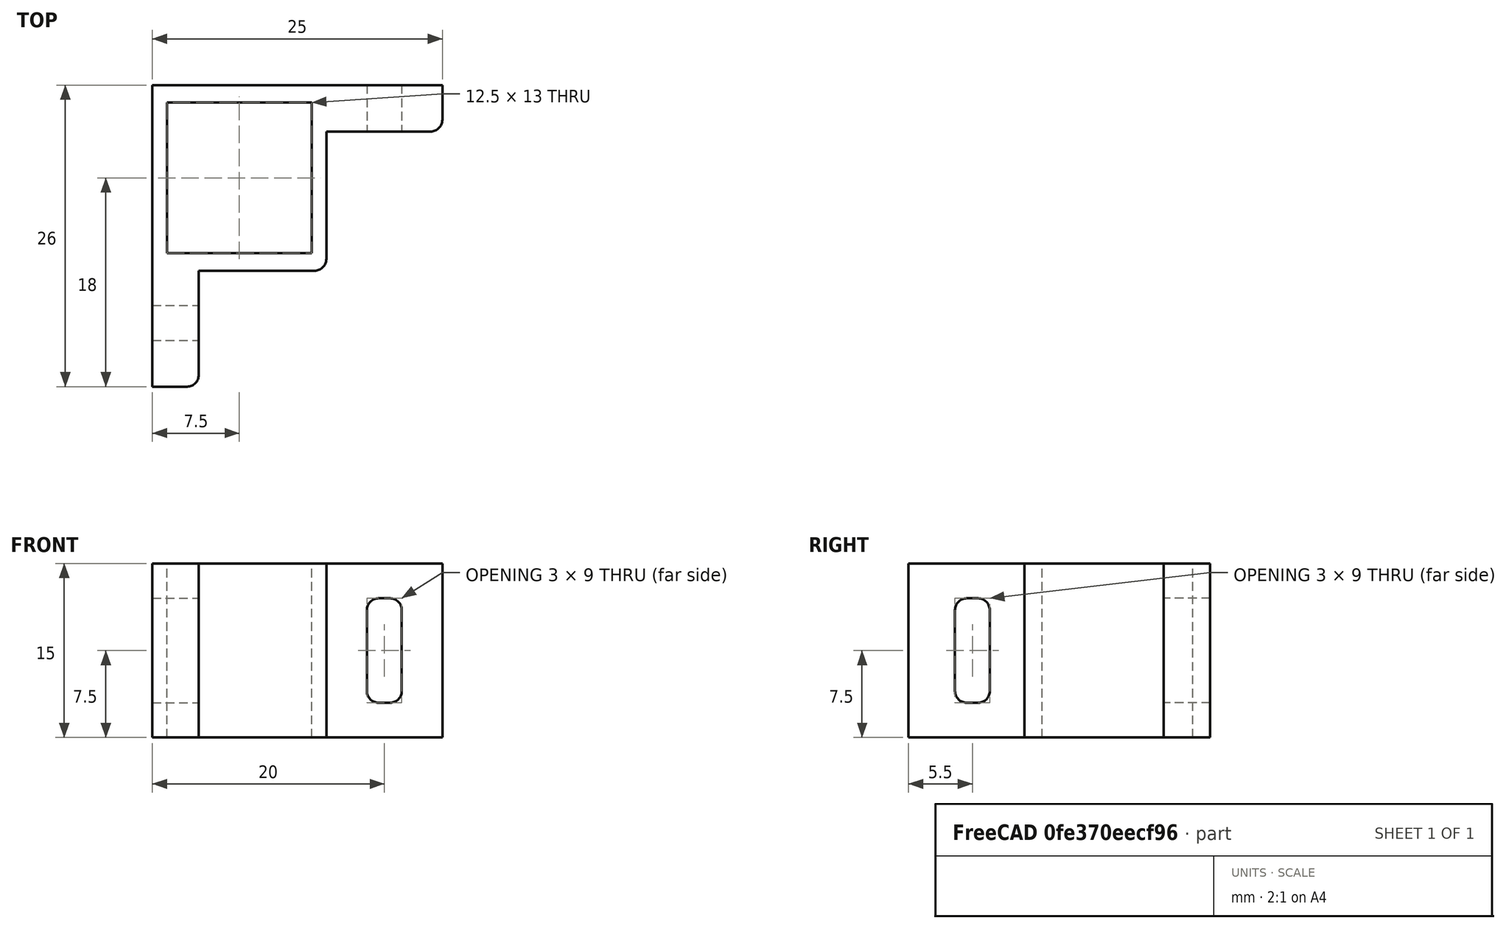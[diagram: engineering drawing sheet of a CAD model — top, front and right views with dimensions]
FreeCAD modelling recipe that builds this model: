
FCSTD DOCUMENT  (FreeCAD 0.14R3402 (Git))
Label: DoorSwitchClamp
License: CC-BY 3.0
LicenseURL: http://creativecommons.org/licenses/by/3.0/
objects: Part::Box×6, Part::Fillet×5, Part::Cut×3, Part::MultiFuse×1
note: 15 computed .brp shape members not serialized (recipe doc carries the construction recipe); baked Part::Feature solids carry a one-line shape summary decoded from their .brp

FEATURE [Part::Box] Box  label="Cube"
  Height = 16
  Length = 15
  Width = 15
FEATURE [Part::Box] Box001  label="Cube001"
  Height = 13
  Length = 12.5
  Placement = pos=(1.25,0,1.5) rot=(0,0,1;0rad)
  Width = 15
FEATURE [Part::Cut] Cut
  Base = -> Box
  Tool = -> Box001
FEATURE [Part::Box] Box002  label="Cube002"
  Height = 10
  Length = 4
  Placement = pos=(0,0,16) rot=(0,0,1;0rad)
  Width = 15
FEATURE [Part::Box] Box003  label="Cube003"
  Height = 4
  Length = 10
  Placement = pos=(15,0,0) rot=(0,0,1;0rad)
  Width = 15
FEATURE [Part::Box] Box004  label="Cube004"
  Height = 3
  Length = 4
  Placement = pos=(0,3,19) rot=(0,0,1;0rad)
  Width = 9
FEATURE [Part::Fillet] Fillet
  Base = -> Box004
  Edges = 4 edges r=1: [Edge9,Edge10,Edge11,Edge12]
FEATURE [Part::Cut] Cut001
  Base = -> Box002
  Tool = -> Fillet
FEATURE [Part::Box] Box005  label="Cube005"
  Height = 4
  Length = 3
  Placement = pos=(18.5,3,0) rot=(0,0,1;0rad)
  Width = 9
FEATURE [Part::Fillet] Fillet001
  Base = -> Box005
  Edges = 4 edges r=1: [Edge1,Edge3,Edge5,Edge7]
FEATURE [Part::Cut] Cut002
  Base = -> Box003
  Tool = -> Fillet001
FEATURE [Part::Fillet] Fillet002
  Base = -> Cut001
  Edges = 1 edges r=1: [Edge17]
FEATURE [Part::Fillet] Fillet003
  Base = -> Cut002
  Edges = 1 edges r=1: [Edge9]
FEATURE [Part::Fillet] Fillet004
  Base = -> Cut
  Edges = 1 edges r=1: [Edge13]
FEATURE [Part::MultiFuse] Fusion
  Placement = pos=(0,0,0) rot=(1,0,0;1.5708rad)
  Shapes = -> [Fillet002,Fillet003,Fillet004]
